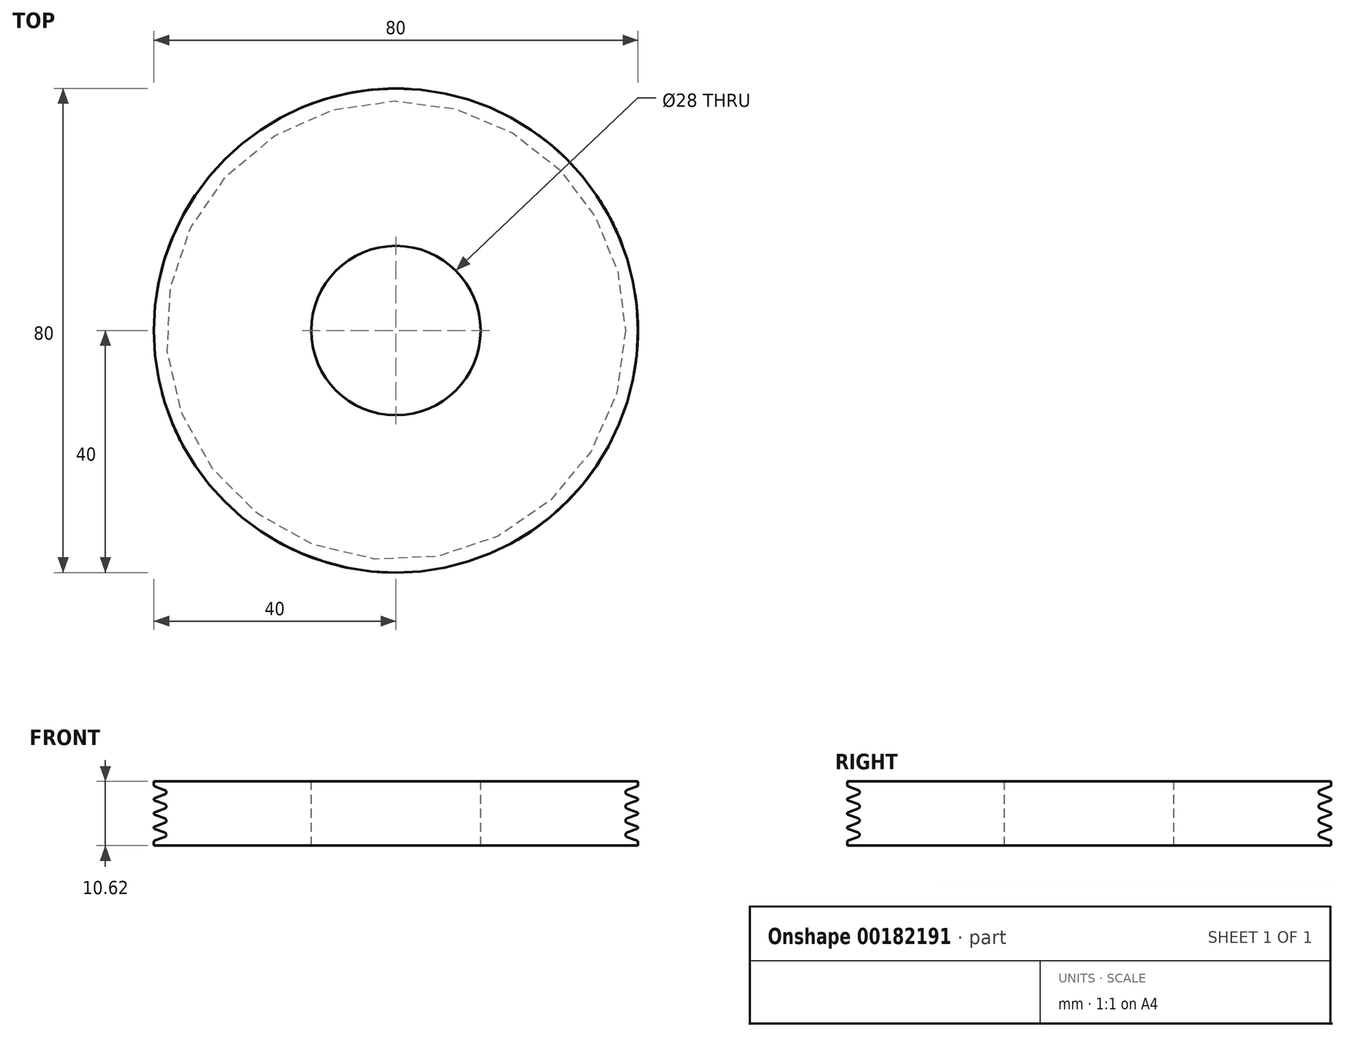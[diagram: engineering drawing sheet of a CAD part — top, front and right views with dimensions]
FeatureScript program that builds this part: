
annotation { "Feature Type Name" : "Feature", "Feature Type Description" : "" }
export const myFeature = defineFeature(function(context is Context, id is Id, definition is map)
    precondition{}
    {
        {
            var Q0;
            Q0=qCreatedBy(makeId("Front.planeOp"),FACE);
            var sketch = newSketch(context, id + "F0", { "sketchPlane" : qUnion([Q0])});
            skArc(sketch, "E0", {"start": v(0.14, -0.38) * mm, "mid": v(0.4, 0) * mm, "end": v(0.14, 0.38) * mm});
            skArc(sketch, "E1", {"start": v(-1.53, -0.98) * mm, "mid": v(-1.66, -1.17) * mm, "end": v(-1.53, -1.36) * mm});
            skLineSegment(sketch, "E2", {"start": v(-1.53, -0.98) * mm, "end": v(0.14, -0.38) * mm});
            skLineSegment(sketch, "E3", {"start": v(1.26, 0) * mm, "end": v(-2.7, 0) * mm, "construction": true});
            skLineSegment(sketch, "E4", {"start": v(-2.84, -1.17) * mm, "end": v(1.4, -1.17) * mm, "construction": true});
            skLineSegment(sketch, "E5.MirrorCS", {"start": v(-1.53, -1.36) * mm, "end": v(0.14, -1.96) * mm});
            skArc(sketch, "E6.MirrorC", {"start": v(0.14, -1.96) * mm, "mid": v(0.4, -2.34) * mm, "end": v(0.14, -2.72) * mm});
            skLineSegment(sketch, "E7", {"start": v(-2.66, -2.34) * mm, "end": v(1.83, -2.34) * mm, "construction": true});
            skArc(sketch, "E8.MirrorC", {"start": v(0.14, -2.72) * mm, "mid": v(0.4, -2.34) * mm, "end": v(0.14, -1.96) * mm});
            skLineSegment(sketch, "E9.MirrorCS", {"start": v(-1.53, -3.32) * mm, "end": v(0.14, -2.72) * mm});
            skArc(sketch, "E10.MirrorC", {"start": v(-1.66, -3.51) * mm, "mid": v(-1.62, -3.4) * mm, "end": v(-1.53, -3.32) * mm});
            skArc(sketch, "E11.MirrorCS", {"start": v(0.14, 1.96) * mm, "mid": v(0.4, 2.34) * mm, "end": v(0.14, 2.72) * mm});
            skArc(sketch, "E12.MirrorCS", {"start": v(-1.53, 0.98) * mm, "mid": v(-1.66, 1.17) * mm, "end": v(-1.53, 1.36) * mm});
            skArc(sketch, "E13.MirrorCS", {"start": v(0.14, 2.72) * mm, "mid": v(0.4, 2.34) * mm, "end": v(0.14, 1.96) * mm});
            skLineSegment(sketch, "E14.MirrorCS", {"start": v(-1.53, 0.98) * mm, "end": v(0.14, 0.38) * mm});
            skArc(sketch, "E15.MirrorC", {"start": v(-1.53, 3.7) * mm, "mid": v(-1.66, 3.5) * mm, "end": v(-1.53, 3.32) * mm});
            skLineSegment(sketch, "E16.MirrorCS", {"start": v(-1.53, 3.32) * mm, "end": v(0.14, 2.72) * mm});
            skLineSegment(sketch, "E17.MirrorCS", {"start": v(-1.53, 1.36) * mm, "end": v(0.14, 1.96) * mm});
            skPoint(sketch, "E18", {"position": v(0.14, 0.38) * mm});
            skLineSegment(sketch, "E19", {"start": v(-1.66, -3.51) * mm, "end": v(-1.66, -4.14) * mm});
            skLineSegment(sketch, "E20", {"start": v(-2.76, 2.34) * mm, "end": v(1.43, 2.34) * mm, "construction": true});
            skLineSegment(sketch, "E21.MirrorCS", {"start": v(-1.53, 3.7) * mm, "end": v(0.14, 4.3) * mm});
            skArc(sketch, "E22.MirrorCS", {"start": v(0.14, 5.06) * mm, "mid": v(0.4, 4.68) * mm, "end": v(0.14, 4.3) * mm});
            skLineSegment(sketch, "E23.MirrorCS", {"start": v(-1.53, 5.66) * mm, "end": v(0.14, 5.06) * mm});
            skArc(sketch, "E24.MirrorCS", {"start": v(-1.53, 5.66) * mm, "mid": v(-1.62, 5.74) * mm, "end": v(-1.66, 5.85) * mm});
            skLineSegment(sketch, "E25", {"start": v(-1.66, 5.85) * mm, "end": v(-1.66, 6.48) * mm});
            skLineSegment(sketch, "E26", {"start": v(-1.66, 6.48) * mm, "end": v(24.34, 6.48) * mm});
            skLineSegment(sketch, "E27", {"start": v(24.34, 6.48) * mm, "end": v(38.34, 6.48) * mm, "construction": true});
            skLineSegment(sketch, "E28", {"start": v(38.34, 6.48) * mm, "end": v(38.34, -4.14) * mm, "construction": true});
            skLineSegment(sketch, "E29", {"start": v(38.34, -4.14) * mm, "end": v(24.34, -4.14) * mm, "construction": true});
            skLineSegment(sketch, "E30", {"start": v(24.34, -4.14) * mm, "end": v(-1.66, -4.14) * mm});
            skLineSegment(sketch, "E31", {"start": v(24.34, 6.48) * mm, "end": v(24.34, -4.14) * mm});
            skPoint(sketch, "E32", {"position": v(0.4, -2.34) * mm});
            skLineSegment(sketch, "E33", {"start": v(0.4, -2.34) * mm, "end": v(0.4, -4.14) * mm, "construction": true});
            skLineSegment(sketch, "E34", {"start": v(-1.53, -3.32) * mm, "end": v(-2.96, -3.84) * mm, "construction": true});
            skLineSegment(sketch, "E35", {"start": v(-1.66, -3.51) * mm, "end": v(-1.66, -0.37) * mm, "construction": true});
            skPoint(sketch, "E36", {"position": v(-1.66, -3.37) * mm});
            skPoint(sketch, "E37", {"position": v(-1.66, -1.17) * mm});
            skLineSegment(sketch, "E38", {"start": v(-1.53, -0.98) * mm, "end": v(-2.66, -1.4) * mm, "construction": true});
            skLineSegment(sketch, "E39", {"start": v(-1.53, -1.36) * mm, "end": v(-2.67, -0.94) * mm, "construction": true});
            skPoint(sketch, "E40", {"position": v(-1.66, -1.03) * mm});
            skPoint(sketch, "E41", {"position": v(-1.66, -1.31) * mm});
            skLineSegment(sketch, "E42", {"start": v(0.14, -1.96) * mm, "end": v(2.64, -2.88) * mm, "construction": true});
            skLineSegment(sketch, "E43", {"start": v(0.14, -2.72) * mm, "end": v(2.38, -1.9) * mm, "construction": true});
            skPoint(sketch, "E44", {"position": v(1.17, -2.34) * mm});
            skLineSegment(sketch, "E45", {"start": v(1.17, -2.34) * mm, "end": v(1.17, -4.14) * mm, "construction": true});
            skSolve(sketch);
        }
        {
            var Q0;
            Q0=makeQuery(id+"F0.imprint","IMPRINT",FACE,{"disambiguationData":[TD([[makeQuery(id+"F0.imprint","IMPRINT",EDGE,{"derivedFrom":sQuery(id+"F0.wireOp",EDGE,"E0")}),-1.0]])]});
            var Q1;
            Q1=sQuery(id+"F0.wireOp",EDGE,"E28");
            revolve(context, id + "F1", {"entities" : qUnion([Q0]), "axis" : qUnion([Q1]), "revolveType" : RevolveType.FULL});
        }
    });
